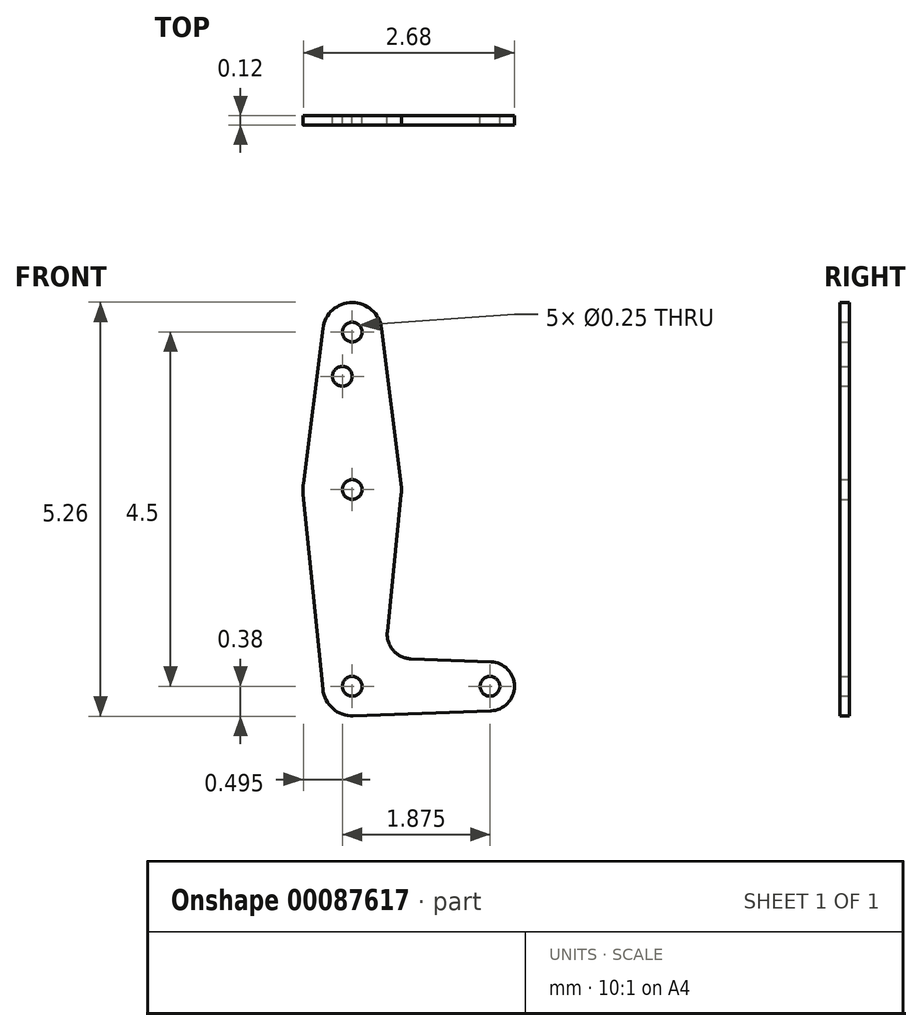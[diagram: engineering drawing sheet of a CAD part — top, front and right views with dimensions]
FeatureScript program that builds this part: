
annotation { "Feature Type Name" : "Feature", "Feature Type Description" : "" }
export const myFeature = defineFeature(function(context is Context, id is Id, definition is map)
    precondition{}
    {
        {
            var Q0;
            Q0=qCreatedBy(makeId("Front.planeOp"),FACE);
            var sketch = newSketch(context, id + "F0", { "sketchPlane" : qUnion([Q0])});
            skLineSegment(sketch, "E0", {"start": v(0, 0) * mm, "end": v(1.75, 0) * mm, "construction": true});
            skLineSegment(sketch, "E1", {"start": v(0, 0) * mm, "end": v(0, 4.5) * mm, "construction": true});
            skCircle(sketch, "E2", {"center": v(1.75, 0) * mm, "radius": 0.31 * mm});
            skCircle(sketch, "E3", {"center": v(0, 0) * mm, "radius": 0.38 * mm});
            skCircle(sketch, "E4", {"center": v(0, 4.5) * mm, "radius": 0.38 * mm});
            skCircle(sketch, "E5", {"center": v(0, 2.5) * mm, "radius": 0.62 * mm});
            skLineSegment(sketch, "E6", {"start": v(0.37, 4.55) * mm, "end": v(0.62, 2.58) * mm});
            skLineSegment(sketch, "E7", {"start": v(-0.62, 2.58) * mm, "end": v(-0.37, 4.55) * mm});
            skLineSegment(sketch, "E8", {"start": v(1.76, 0.31) * mm, "end": v(0.75, 0.35) * mm});
            skLineSegment(sketch, "E9", {"start": v(1.76, -0.31) * mm, "end": v(0.01, -0.37) * mm});
            skLineSegment(sketch, "E10", {"start": v(0.62, 2.44) * mm, "end": v(0.45, 0.7) * mm});
            skLineSegment(sketch, "E11", {"start": v(-0.62, 2.44) * mm, "end": v(-0.37, -0.04) * mm});
            skCircle(sketch, "E12", {"center": v(-0.12, 3.94) * mm, "radius": 0.12 * mm});
            skCircle(sketch, "E13", {"center": v(0, 4.5) * mm, "radius": 0.12 * mm});
            skCircle(sketch, "E14", {"center": v(0, 0) * mm, "radius": 0.12 * mm});
            skCircle(sketch, "E15", {"center": v(1.75, 0) * mm, "radius": 0.12 * mm});
            skArc(sketch, "E16.filletArc", {"start": v(0.45, 0.7) * mm, "mid": v(0.52, 0.46) * mm, "end": v(0.75, 0.35) * mm});
            skCircle(sketch, "E17", {"center": v(0, 2.5) * mm, "radius": 0.12 * mm});
            skSolve(sketch);
        }
        {
            var Q0;
            Q0 = qSketchRegion(id + "F0", true);
            extrude(context, id + "F1", {"entities" : qUnion([Q0]), "depth" : 0.12 * mm});
        }
    });
